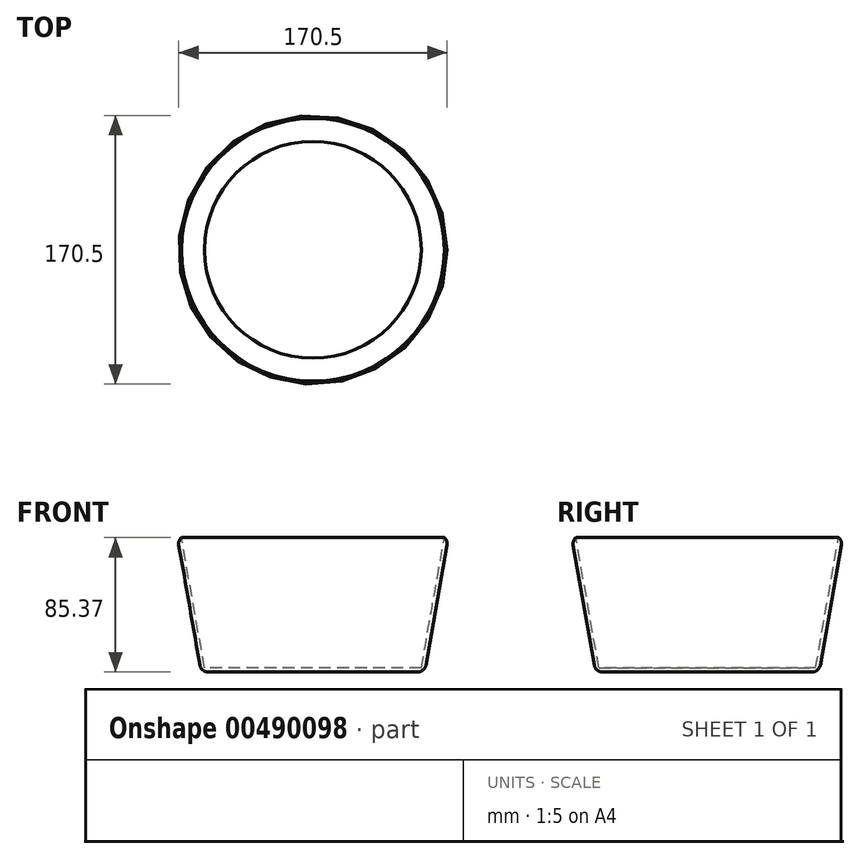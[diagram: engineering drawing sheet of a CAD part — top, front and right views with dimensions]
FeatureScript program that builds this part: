
annotation { "Feature Type Name" : "Feature", "Feature Type Description" : "" }
export const myFeature = defineFeature(function(context is Context, id is Id, definition is map)
    precondition{}
    {
        {
            var Q0;
            Q0=qCreatedBy(makeId("Top.planeOp"),FACE);
            var sketch = newSketch(context, id + "F0", { "sketchPlane" : qUnion([Q0])});
            skCircle(sketch, "E0", {"center": v(34.4, 0) * mm, "radius": 41.2 * mm});
            skCircle(sketch, "E1", {"center": v(-26.35, -54.18) * mm, "radius": 41.78 * mm});
            skCircle(sketch, "E2", {"center": v(-58.16, 94.14) * mm, "radius": 70.96 * mm});
            skCircle(sketch, "E3", {"center": v(100.69, -159.13) * mm, "radius": 51.54 * mm});
            skCircle(sketch, "E4", {"center": v(128.48, -11.77) * mm, "radius": 115.99 * mm});
            skSolve(sketch);
        }
        {
            var Q0;
            Q0=makeQuery(id+"F0.imprint","IMPRINT",FACE,{"disambiguationData":[TD([[makeQuery(id+"F0.imprint","IMPRINT",EDGE,{"derivedFrom":sQuery(id+"F0.wireOp",EDGE,"E2")}),1.0]])]});
            extrude(context, id + "F1", {"entities" : qUnion([Q0]), "depth" : 85.37 * mm, "hasDraft" : true, "draftAngle" : 10 * degree});
        }
        {
            var Q0;
            Q0=makeQuery(id+"F1.opExtrude","CAP_FACE",FACE,{"disambiguationData":[OSD([sQuery(id+"F0.wireOp",EDGE,"E2")])],"isStart":false});
            shell(context, id + "F2", {"entities" : qUnion([Q0]), "thickness" : 2.54 * mm});
        }
        {
            var Q0;
            Q0=makeQuery(id+"F1.opExtrude","SWEPT_FACE",FACE,{"disambiguationData":[OSD([sQuery(id+"F0.wireOp",EDGE,"E2")])]});
            var Q1;
            Q1=makeQuery(id+"F1.opExtrude","CAP_EDGE",EDGE,{"disambiguationData":[OSD([sQuery(id+"F0.wireOp",EDGE,"E2")])],"isStart":true});
            fillet(context, id + "F3", {"entities" : qUnion([Q0, Q1]), "radius" : 5.08 * mm, "tangentPropagation" : true, "allowEdgeOverflow" : false});
        }
    });
